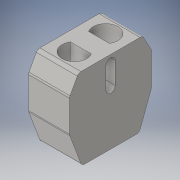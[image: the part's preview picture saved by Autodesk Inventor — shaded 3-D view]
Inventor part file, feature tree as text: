
AUTODESK INVENTOR PART (.ipt)
format: ipt  version: 2016 (Build 200138000, 138)  size: 206,848 bytes
history: native  units: in
note: dims shown in document units (in); Inventor stores cm internally (conversion verified against a paired STEP export)
features: sketch x12, extrude x9, revolve x2, plane x1, fillet x1
ambient origin geometry x8: Origin, YZ Plane, XZ Plane, XY Plane, X Axis, Y Axis, Z Axis, Center Point
bodies: Solid1 (feature_tree)
feature tree (25):
  extrude  "Extrusion1"  Depth=1.0in
  sketch  "Sketch2"  dims[d2=0.5in d3=0.0in d4=0.04in]
  plane  "Work Plane1"
  revolve  "Revolution1"  [1 undecoded]
  revolve  "Revolution2"  Angle=90.0deg
  extrude  "Extrusion2"  TaperAngle=90.0deg  [1 undecoded]
  extrude  "Extrusion3"  Depth=0.15in
  extrude  "Extrusion4"  Depth=0.15in
  extrude  "Extrusion5"  Depth=0.5in TaperAngle=0.0deg
  extrude  "Extrusion6"  Depth=0.11in
  extrude  "Extrusion7"  Depth=0.11in
  extrude  "Extrusion8"  Depth=0.5in TaperAngle=0.0deg
  extrude  "Extrusion9"  Depth=0.5in TaperAngle=0.0deg
  fillet  "Fillet1"  Radius=0.5in
  sketch  "Sketch1"  dims[d0=1.0in d1=1.0in]
  sketch  "Sketch3"  dims[d5=0.04in d6=90.0deg]
  sketch  "Sketch4"  dims[d7=0.3in d8=90.0deg]
  sketch  "Sketch5"  dims[d9=0.15in d10=0.4in]
  sketch  "Sketch6"  dims[d11=0.5in d12=0.0in d13=0.15in]
  sketch  "Sketch7"  dims[d14=0.4in d15=0.5in d16=0.0in]
  sketch  "Sketch8"  dims[d17=0.11in d18=0.2in]
  sketch  "Sketch9"  dims[d19=0.5in d20=0.0in d21=0.11in]
  sketch  "Sketch10"  dims[d22=0.2in d23=0.5in d24=0.0in]
  sketch  "Sketch11"  dims[d25=0.5in d26=0.0in d28=0.5in d29=0.0in d30=0.5in d31=0.0in]
  sketch  "Sketch12"  dims[d32=0.112in d33=1.0in d34=0.0in d35=0.05in]
note: 2 required parameter values undecoded (feature->parameter linkage not recoverable at this tier; creation-order binding heuristic only, values carry confidence <= 0.55)